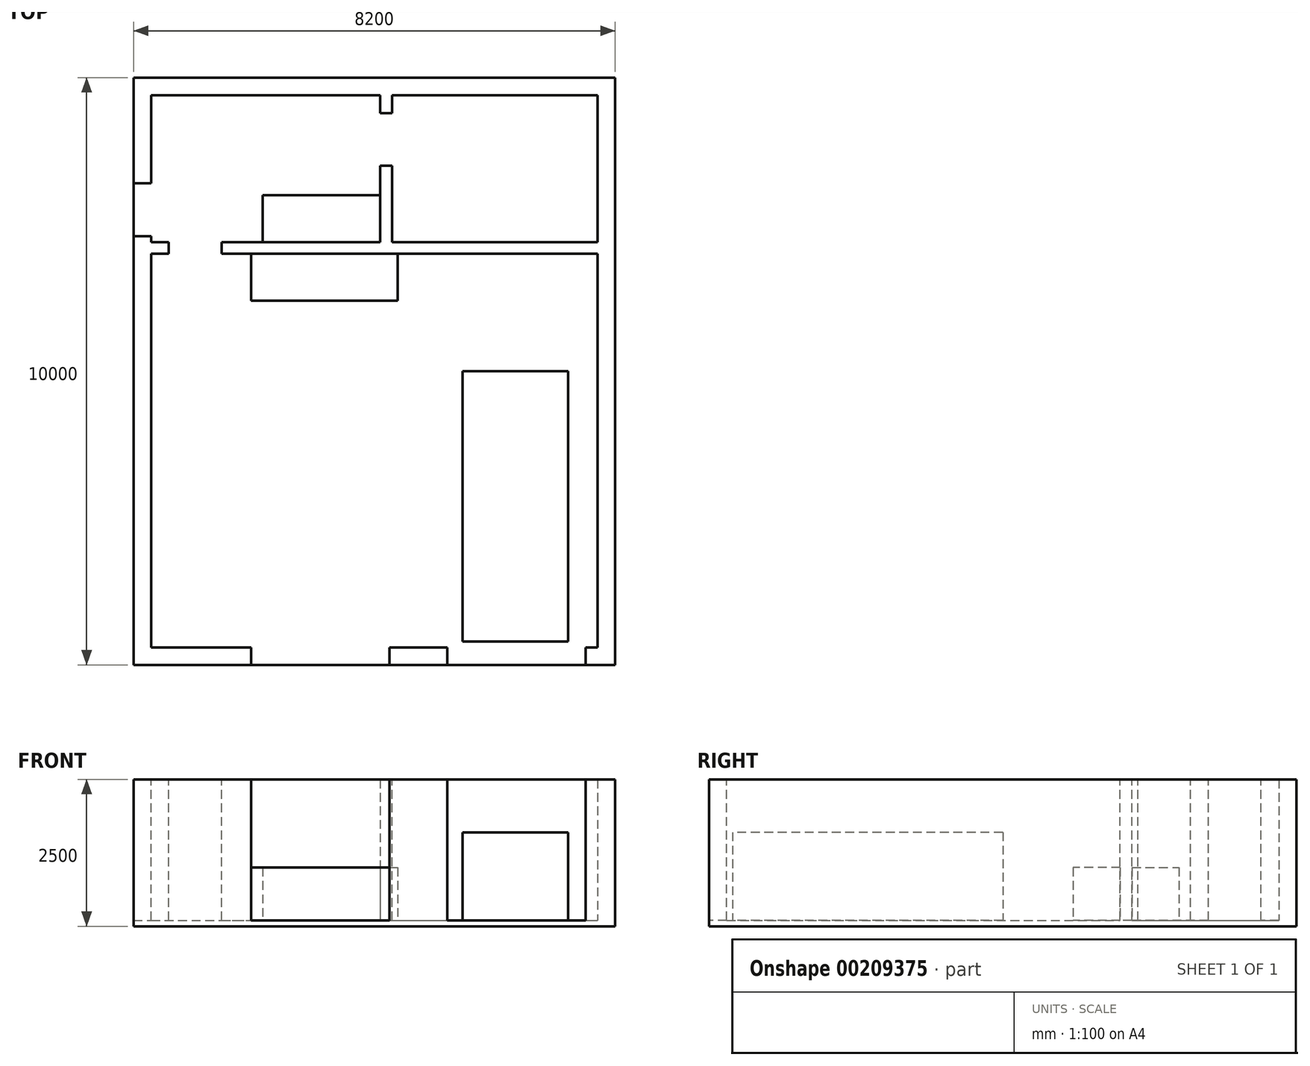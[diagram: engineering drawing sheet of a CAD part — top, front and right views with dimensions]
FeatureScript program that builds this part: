
annotation { "Feature Type Name" : "Feature", "Feature Type Description" : "" }
export const myFeature = defineFeature(function(context is Context, id is Id, definition is map)
    precondition{}
    {
        {
            var Q0;
            Q0=qCreatedBy(makeId("Top.planeOp"),FACE);
            var sketch = newSketch(context, id + "F0", { "sketchPlane" : qUnion([Q0])});
            skLineSegment(sketch, "E0.bottom", {"start": v(0, 0) * mm, "end": v(8200, 0) * mm});
            skLineSegment(sketch, "E0.top", {"start": v(0, 10000) * mm, "end": v(8200, 10000) * mm});
            skLineSegment(sketch, "E0.left", {"start": v(0, 0) * mm, "end": v(0, 10000) * mm});
            skLineSegment(sketch, "E0.right", {"start": v(8200, 0) * mm, "end": v(8200, 10000) * mm});
            skSolve(sketch);
        }
        {
            var Q0;
            Q0=makeQuery(id+"F0.imprint","IMPRINT",FACE,{"disambiguationData":[TD([[makeQuery(id+"F0.imprint","IMPRINT",EDGE,{"derivedFrom":sQuery(id+"F0.wireOp",EDGE,"E0.bottom")}),1.0]])]});
            var sketch = newSketch(context, id + "F1", { "sketchPlane" : qUnion([Q0])});
            skLineSegment(sketch, "E1.bottom", {"start": v(300, 300) * mm, "end": v(7900, 300) * mm});
            skLineSegment(sketch, "E1.top", {"start": v(300, 9700) * mm, "end": v(7900, 9700) * mm});
            skLineSegment(sketch, "E1.left", {"start": v(300, 300) * mm, "end": v(300, 9700) * mm});
            skLineSegment(sketch, "E1.right", {"start": v(7900, 300) * mm, "end": v(7900, 9700) * mm});
            skSolve(sketch);
        }
        {
            var Q0;
            Q0=makeQuery(id+"F0.imprint","IMPRINT",FACE,{"disambiguationData":[TD([[makeQuery(id+"F0.imprint","IMPRINT",EDGE,{"derivedFrom":sQuery(id+"F0.wireOp",EDGE,"E0.bottom")}),1.0]])]});
            var sketch = newSketch(context, id + "F2", { "sketchPlane" : qUnion([Q0])});
            skLineSegment(sketch, "E2", {"start": v(2000, 300) * mm, "end": v(2000, 0) * mm});
            skLineSegment(sketch, "E3", {"start": v(2000, 0) * mm, "end": v(4360, 0) * mm});
            skLineSegment(sketch, "E4", {"start": v(4360, 0) * mm, "end": v(4360, 300) * mm});
            skLineSegment(sketch, "E5", {"start": v(4360, 300) * mm, "end": v(2000, 300) * mm});
            skLineSegment(sketch, "E6.bottom", {"start": v(5340, 0) * mm, "end": v(7700, 0) * mm});
            skLineSegment(sketch, "E6.top", {"start": v(5340, 300) * mm, "end": v(7700, 300) * mm});
            skLineSegment(sketch, "E6.left", {"start": v(5340, 0) * mm, "end": v(5340, 300) * mm});
            skLineSegment(sketch, "E6.right", {"start": v(7700, 0) * mm, "end": v(7700, 300) * mm});
            skSolve(sketch);
        }
        {
            var Q0;
            Q0 = qSketchRegion(id + "F0", true);
            extrude(context, id + "F3", {"entities" : qUnion([Q0]), "oppositeDirection" : true, "depth" : 2500 * mm});
        }
        {
            var Q0;
            Q0 = qSketchRegion(id + "F1", true);
            extrude(context, id + "F4", {"entities" : qUnion([Q0]), "operationType" : NewBodyOperationType.REMOVE, "oppositeDirection" : true, "depth" : 2400 * mm});
        }
        {
            var Q0;
            Q0 = qSketchRegion(id + "F2", true);
            extrude(context, id + "F5", {"entities" : qUnion([Q0]), "operationType" : NewBodyOperationType.REMOVE, "oppositeDirection" : true, "depth" : 2400 * mm});
        }
        {
            var Q0;
            Q0=makeQuery(id+"F5.boolean.opBoolean","MERGE",FACE,{"derivedFrom":[makeQuery(id+"F4.boolean.opBoolean","COPY",FACE,{"derivedFrom":makeQuery(id+"F4.opExtrude","CAP_FACE",FACE,{"disambiguationData":[OSD([sQuery(id+"F1.wireOp",EDGE,"E1.bottom"),sQuery(id+"F1.wireOp",EDGE,"E1.top"),sQuery(id+"F1.wireOp",EDGE,"E1.left"),sQuery(id+"F1.wireOp",EDGE,"E1.right")])],"isStart":false})}),makeQuery(id+"F5.opExtrude","CAP_FACE",FACE,{"disambiguationData":[OSD([sQuery(id+"F2.wireOp",EDGE,"E2"),sQuery(id+"F2.wireOp",EDGE,"E3"),sQuery(id+"F2.wireOp",EDGE,"E4"),sQuery(id+"F2.wireOp",EDGE,"E5")])],"isStart":false}),makeQuery(id+"F5.opExtrude","CAP_FACE",FACE,{"disambiguationData":[OSD([sQuery(id+"F2.wireOp",EDGE,"E6.bottom"),sQuery(id+"F2.wireOp",EDGE,"E6.top"),sQuery(id+"F2.wireOp",EDGE,"E6.left"),sQuery(id+"F2.wireOp",EDGE,"E6.right")])],"isStart":false})]});
            var sketch = newSketch(context, id + "F6", { "sketchPlane" : qUnion([Q0])});
            skLineSegment(sketch, "E7.bottom", {"start": v(300, 7200) * mm, "end": v(7900, 7200) * mm});
            skLineSegment(sketch, "E7.top", {"start": v(300, 7000) * mm, "end": v(7900, 7000) * mm});
            skLineSegment(sketch, "E7.left", {"start": v(300, 7200) * mm, "end": v(300, 7000) * mm});
            skLineSegment(sketch, "E7.right", {"start": v(7900, 7200) * mm, "end": v(7900, 7000) * mm});
            skSolve(sketch);
        }
        {
            var Q0;
            Q0=makeQuery(id+"F6.imprint","IMPRINT",FACE,{"disambiguationData":[TD([[makeQuery(id+"F6.imprint","IMPRINT",EDGE,{"derivedFrom":sQuery(id+"F6.wireOp",EDGE,"E7.bottom")}),-1.0]])]});
            extrude(context, id + "F7", {"entities" : qUnion([Q0]), "operationType" : NewBodyOperationType.ADD, "depth" : 2400 * mm});
        }
        {
            var Q0;
            {var subQ0=sQuery(id+"F1.wireOp",EDGE,"E1.top");var subQ1=sQuery(id+"F1.wireOp",EDGE,"E1.left");var subQ2=sQuery(id+"F1.wireOp",EDGE,"E1.right");Q0=makeQuery(id+"F7.boolean.opBoolean","SPLIT",FACE,{"disambiguationData":[TD([makeQuery(id+"F4.boolean.opBoolean","COPY",FACE,{"derivedFrom":makeQuery(id+"F4.opExtrude","SWEPT_FACE",FACE,{"disambiguationData":[OSD([subQ0])]})})])],"derivedFrom":makeQuery(id+"F5.boolean.opBoolean","MERGE",FACE,{"derivedFrom":[makeQuery(id+"F4.boolean.opBoolean","COPY",FACE,{"derivedFrom":makeQuery(id+"F4.opExtrude","CAP_FACE",FACE,{"disambiguationData":[OSD([sQuery(id+"F1.wireOp",EDGE,"E1.bottom"),subQ0,subQ1,subQ2])],"isStart":false})}),makeQuery(id+"F5.opExtrude","CAP_FACE",FACE,{"disambiguationData":[OSD([sQuery(id+"F2.wireOp",EDGE,"E2"),sQuery(id+"F2.wireOp",EDGE,"E3"),sQuery(id+"F2.wireOp",EDGE,"E4"),sQuery(id+"F2.wireOp",EDGE,"E5")])],"isStart":false}),makeQuery(id+"F5.opExtrude","CAP_FACE",FACE,{"disambiguationData":[OSD([sQuery(id+"F2.wireOp",EDGE,"E6.bottom"),sQuery(id+"F2.wireOp",EDGE,"E6.top"),sQuery(id+"F2.wireOp",EDGE,"E6.left"),sQuery(id+"F2.wireOp",EDGE,"E6.right")])],"isStart":false})]})});}
            var sketch = newSketch(context, id + "F8", { "sketchPlane" : qUnion([Q0])});
            skLineSegment(sketch, "E8.bottom", {"start": v(4200, 9700) * mm, "end": v(4400, 9700) * mm});
            skLineSegment(sketch, "E8.top", {"start": v(4200, 7200) * mm, "end": v(4400, 7200) * mm});
            skLineSegment(sketch, "E8.left", {"start": v(4200, 9700) * mm, "end": v(4200, 7200) * mm});
            skLineSegment(sketch, "E8.right", {"start": v(4400, 9700) * mm, "end": v(4400, 7200) * mm});
            skSolve(sketch);
        }
        {
            var Q0;
            Q0 = qSketchRegion(id + "F8", true);
            extrude(context, id + "F9", {"entities" : qUnion([Q0]), "operationType" : NewBodyOperationType.ADD, "depth" : 2400 * mm});
        }
        {
            var Q0;
            {var subQ0=sQuery(id+"F0.wireOp",EDGE,"E0.right");var subQ1=sQuery(id+"F0.wireOp",EDGE,"E0.left");var subQ2=sQuery(id+"F0.wireOp",EDGE,"E0.top");var subQ3=sQuery(id+"F0.wireOp",EDGE,"E0.bottom");Q0=makeQuery(id+"F9.boolean.opBoolean","MERGE",FACE,{"derivedFrom":[makeQuery(id+"F7.boolean.opBoolean","MERGE",FACE,{"derivedFrom":[makeQuery(id+"F5.boolean.opBoolean","SPLIT",FACE,{"disambiguationData":[TD([makeQuery(id+"F3.opExtrude","SWEPT_FACE",FACE,{"disambiguationData":[OSD([subQ2])]})])],"derivedFrom":makeQuery(id+"F3.opExtrude","CAP_FACE",FACE,{"disambiguationData":[OSD([subQ3,subQ2,subQ1,subQ0])],"isStart":true})}),makeQuery(id+"F7.opExtrude","CAP_FACE",FACE,{"disambiguationData":[OSD([sQuery(id+"F6.wireOp",EDGE,"E7.bottom"),sQuery(id+"F6.wireOp",EDGE,"E7.top"),sQuery(id+"F6.wireOp",EDGE,"E7.left"),sQuery(id+"F6.wireOp",EDGE,"E7.right")])],"isStart":false})]}),makeQuery(id+"F9.opExtrude","CAP_FACE",FACE,{"disambiguationData":[OSD([sQuery(id+"F8.wireOp",EDGE,"E8.bottom"),sQuery(id+"F8.wireOp",EDGE,"E8.top"),sQuery(id+"F8.wireOp",EDGE,"E8.left"),sQuery(id+"F8.wireOp",EDGE,"E8.right")])],"isStart":false})]});}
            var sketch = newSketch(context, id + "F10", { "sketchPlane" : qUnion([Q0])});
            skLineSegment(sketch, "E9.bottom", {"start": v(0, 8200) * mm, "end": v(300, 8200) * mm});
            skLineSegment(sketch, "E9.top", {"start": v(0, 7300) * mm, "end": v(300, 7300) * mm});
            skLineSegment(sketch, "E9.left", {"start": v(0, 8200) * mm, "end": v(0, 7300) * mm});
            skLineSegment(sketch, "E9.right", {"start": v(300, 8200) * mm, "end": v(300, 7300) * mm});
            skLineSegment(sketch, "E10.bottom", {"start": v(600, 7200) * mm, "end": v(1500, 7200) * mm});
            skLineSegment(sketch, "E10.top", {"start": v(600, 7000) * mm, "end": v(1500, 7000) * mm});
            skLineSegment(sketch, "E10.left", {"start": v(600, 7200) * mm, "end": v(600, 7000) * mm});
            skLineSegment(sketch, "E10.right", {"start": v(1500, 7200) * mm, "end": v(1500, 7000) * mm});
            skLineSegment(sketch, "E11.bottom", {"start": v(4200, 9400) * mm, "end": v(4400, 9400) * mm});
            skLineSegment(sketch, "E11.top", {"start": v(4200, 8500) * mm, "end": v(4400, 8500) * mm});
            skLineSegment(sketch, "E11.left", {"start": v(4200, 9400) * mm, "end": v(4200, 8500) * mm});
            skLineSegment(sketch, "E11.right", {"start": v(4400, 9400) * mm, "end": v(4400, 8500) * mm});
            skSolve(sketch);
        }
        {
            var Q0;
            Q0=makeQuery(id+"F10.imprint","IMPRINT",FACE,{"disambiguationData":[TD([[makeQuery(id+"F10.imprint","IMPRINT",EDGE,{"derivedFrom":sQuery(id+"F10.wireOp",EDGE,"E10.bottom")}),-1.0]])]});
            var Q1;
            Q1=makeQuery(id+"F10.imprint","IMPRINT",FACE,{"disambiguationData":[TD([[makeQuery(id+"F10.imprint","IMPRINT",EDGE,{"derivedFrom":sQuery(id+"F10.wireOp",EDGE,"E11.bottom")}),-1.0]])]});
            var Q2;
            Q2=makeQuery(id+"F10.imprint","IMPRINT",FACE,{"disambiguationData":[TD([[makeQuery(id+"F10.imprint","IMPRINT",EDGE,{"derivedFrom":sQuery(id+"F10.wireOp",EDGE,"E9.bottom")}),-1.0]])]});
            extrude(context, id + "F11", {"entities" : qUnion([Q0, Q1, Q2]), "operationType" : NewBodyOperationType.REMOVE, "oppositeDirection" : true, "depth" : 2400 * mm});
        }
        {
            var Q0;
            {var subQ0=sQuery(id+"F1.wireOp",EDGE,"E1.top");var subQ1=makeQuery(id+"F4.boolean.opBoolean","COPY",FACE,{"derivedFrom":makeQuery(id+"F4.opExtrude","SWEPT_FACE",FACE,{"disambiguationData":[OSD([subQ0])]})});var subQ2=sQuery(id+"F1.wireOp",EDGE,"E1.right");var subQ3=makeQuery(id+"F4.boolean.opBoolean","COPY",FACE,{"derivedFrom":makeQuery(id+"F4.opExtrude","SWEPT_FACE",FACE,{"disambiguationData":[OSD([subQ2])]})});var subQ5=sQuery(id+"F1.wireOp",EDGE,"E1.left");var subQ6=makeQuery(id+"F4.boolean.opBoolean","COPY",FACE,{"derivedFrom":makeQuery(id+"F4.opExtrude","SWEPT_FACE",FACE,{"disambiguationData":[OSD([subQ5])]})});var subQ7=sQuery(id+"F2.wireOp",EDGE,"E6.right");var subQ8=sQuery(id+"F2.wireOp",EDGE,"E6.left");var subQ9=sQuery(id+"F2.wireOp",EDGE,"E4");var subQ10=sQuery(id+"F2.wireOp",EDGE,"E2");var subQ11=sQuery(id+"F1.wireOp",EDGE,"E1.bottom");var subQ12=makeQuery(id+"F5.boolean.opBoolean","MERGE",FACE,{"derivedFrom":[makeQuery(id+"F4.boolean.opBoolean","COPY",FACE,{"derivedFrom":makeQuery(id+"F4.opExtrude","CAP_FACE",FACE,{"disambiguationData":[OSD([subQ11,subQ0,subQ5,subQ2])],"isStart":false})}),makeQuery(id+"F5.opExtrude","CAP_FACE",FACE,{"disambiguationData":[OSD([subQ10,sQuery(id+"F2.wireOp",EDGE,"E3"),subQ9,sQuery(id+"F2.wireOp",EDGE,"E5")])],"isStart":false}),makeQuery(id+"F5.opExtrude","CAP_FACE",FACE,{"disambiguationData":[OSD([sQuery(id+"F2.wireOp",EDGE,"E6.bottom"),sQuery(id+"F2.wireOp",EDGE,"E6.top"),subQ8,subQ7])],"isStart":false})]});var subQ13=makeQuery(id+"F7.boolean.opBoolean","SPLIT",FACE,{"disambiguationData":[TD([subQ1])],"derivedFrom":subQ12});Q0=makeQuery(id+"F11.boolean.opBoolean","MERGE",FACE,{"derivedFrom":[makeQuery(id+"F7.boolean.opBoolean","SPLIT",FACE,{"disambiguationData":[TD([makeQuery(id+"F3.opExtrude","SWEPT_FACE",FACE,{"disambiguationData":[OSD([sQuery(id+"F0.wireOp",EDGE,"E0.bottom")])]})])],"derivedFrom":subQ12}),makeQuery(id+"F9.boolean.opBoolean","SPLIT",FACE,{"disambiguationData":[TD([subQ6])],"derivedFrom":subQ13}),makeQuery(id+"F9.boolean.opBoolean","SPLIT",FACE,{"disambiguationData":[TD([subQ3])],"derivedFrom":subQ13}),makeQuery(id+"F11.opExtrude","CAP_FACE",FACE,{"disambiguationData":[OSD([sQuery(id+"F10.wireOp",EDGE,"E9.bottom"),sQuery(id+"F10.wireOp",EDGE,"E9.top"),sQuery(id+"F10.wireOp",EDGE,"E9.left"),sQuery(id+"F10.wireOp",EDGE,"E9.right")])],"isStart":false}),makeQuery(id+"F11.opExtrude","CAP_FACE",FACE,{"disambiguationData":[OSD([sQuery(id+"F10.wireOp",EDGE,"E10.bottom"),sQuery(id+"F10.wireOp",EDGE,"E10.top"),sQuery(id+"F10.wireOp",EDGE,"E10.left"),sQuery(id+"F10.wireOp",EDGE,"E10.right")])],"isStart":false}),makeQuery(id+"F11.opExtrude","CAP_FACE",FACE,{"disambiguationData":[OSD([sQuery(id+"F10.wireOp",EDGE,"E11.bottom"),sQuery(id+"F10.wireOp",EDGE,"E11.top"),sQuery(id+"F10.wireOp",EDGE,"E11.left"),sQuery(id+"F10.wireOp",EDGE,"E11.right")])],"isStart":false})]});}
            var sketch = newSketch(context, id + "F12", { "sketchPlane" : qUnion([Q0])});
            skLineSegment(sketch, "E12.bottom", {"start": v(2200, 7200) * mm, "end": v(4200, 7200) * mm});
            skLineSegment(sketch, "E12.top", {"start": v(2200, 8000) * mm, "end": v(4200, 8000) * mm});
            skLineSegment(sketch, "E12.left", {"start": v(2200, 7200) * mm, "end": v(2200, 8000) * mm});
            skLineSegment(sketch, "E12.right", {"start": v(4200, 7200) * mm, "end": v(4200, 8000) * mm});
            skSolve(sketch);
        }
        {
            var Q0;
            Q0=makeQuery(id+"F12.imprint","IMPRINT",FACE,{"disambiguationData":[TD([[makeQuery(id+"F12.imprint","IMPRINT",EDGE,{"derivedFrom":sQuery(id+"F12.wireOp",EDGE,"E12.bottom")}),1.0]])]});
            extrude(context, id + "F13", {"entities" : qUnion([Q0]), "depth" : 900 * mm});
        }
        {
            var Q0;
            {var subQ0=sQuery(id+"F1.wireOp",EDGE,"E1.top");var subQ1=makeQuery(id+"F4.boolean.opBoolean","COPY",FACE,{"derivedFrom":makeQuery(id+"F4.opExtrude","SWEPT_FACE",FACE,{"disambiguationData":[OSD([subQ0])]})});var subQ2=sQuery(id+"F1.wireOp",EDGE,"E1.right");var subQ3=makeQuery(id+"F4.boolean.opBoolean","COPY",FACE,{"derivedFrom":makeQuery(id+"F4.opExtrude","SWEPT_FACE",FACE,{"disambiguationData":[OSD([subQ2])]})});var subQ5=sQuery(id+"F1.wireOp",EDGE,"E1.left");var subQ6=makeQuery(id+"F4.boolean.opBoolean","COPY",FACE,{"derivedFrom":makeQuery(id+"F4.opExtrude","SWEPT_FACE",FACE,{"disambiguationData":[OSD([subQ5])]})});var subQ7=sQuery(id+"F2.wireOp",EDGE,"E6.right");var subQ8=sQuery(id+"F2.wireOp",EDGE,"E6.left");var subQ9=sQuery(id+"F2.wireOp",EDGE,"E4");var subQ10=sQuery(id+"F2.wireOp",EDGE,"E2");var subQ11=sQuery(id+"F1.wireOp",EDGE,"E1.bottom");var subQ12=makeQuery(id+"F5.boolean.opBoolean","MERGE",FACE,{"derivedFrom":[makeQuery(id+"F4.boolean.opBoolean","COPY",FACE,{"derivedFrom":makeQuery(id+"F4.opExtrude","CAP_FACE",FACE,{"disambiguationData":[OSD([subQ11,subQ0,subQ5,subQ2])],"isStart":false})}),makeQuery(id+"F5.opExtrude","CAP_FACE",FACE,{"disambiguationData":[OSD([subQ10,sQuery(id+"F2.wireOp",EDGE,"E3"),subQ9,sQuery(id+"F2.wireOp",EDGE,"E5")])],"isStart":false}),makeQuery(id+"F5.opExtrude","CAP_FACE",FACE,{"disambiguationData":[OSD([sQuery(id+"F2.wireOp",EDGE,"E6.bottom"),sQuery(id+"F2.wireOp",EDGE,"E6.top"),subQ8,subQ7])],"isStart":false})]});var subQ13=makeQuery(id+"F7.boolean.opBoolean","SPLIT",FACE,{"disambiguationData":[TD([subQ1])],"derivedFrom":subQ12});Q0=makeQuery(id+"F11.boolean.opBoolean","MERGE",FACE,{"derivedFrom":[makeQuery(id+"F7.boolean.opBoolean","SPLIT",FACE,{"disambiguationData":[TD([makeQuery(id+"F3.opExtrude","SWEPT_FACE",FACE,{"disambiguationData":[OSD([sQuery(id+"F0.wireOp",EDGE,"E0.bottom")])]})])],"derivedFrom":subQ12}),makeQuery(id+"F9.boolean.opBoolean","SPLIT",FACE,{"disambiguationData":[TD([subQ6])],"derivedFrom":subQ13}),makeQuery(id+"F9.boolean.opBoolean","SPLIT",FACE,{"disambiguationData":[TD([subQ3])],"derivedFrom":subQ13}),makeQuery(id+"F11.opExtrude","CAP_FACE",FACE,{"disambiguationData":[OSD([sQuery(id+"F10.wireOp",EDGE,"E9.bottom"),sQuery(id+"F10.wireOp",EDGE,"E9.top"),sQuery(id+"F10.wireOp",EDGE,"E9.left"),sQuery(id+"F10.wireOp",EDGE,"E9.right")])],"isStart":false}),makeQuery(id+"F11.opExtrude","CAP_FACE",FACE,{"disambiguationData":[OSD([sQuery(id+"F10.wireOp",EDGE,"E10.bottom"),sQuery(id+"F10.wireOp",EDGE,"E10.top"),sQuery(id+"F10.wireOp",EDGE,"E10.left"),sQuery(id+"F10.wireOp",EDGE,"E10.right")])],"isStart":false}),makeQuery(id+"F11.opExtrude","CAP_FACE",FACE,{"disambiguationData":[OSD([sQuery(id+"F10.wireOp",EDGE,"E11.bottom"),sQuery(id+"F10.wireOp",EDGE,"E11.top"),sQuery(id+"F10.wireOp",EDGE,"E11.left"),sQuery(id+"F10.wireOp",EDGE,"E11.right")])],"isStart":false})]});}
            var sketch = newSketch(context, id + "F14", { "sketchPlane" : qUnion([Q0])});
            skLineSegment(sketch, "E13.bottom", {"start": v(5600, 5000) * mm, "end": v(7400, 5000) * mm});
            skLineSegment(sketch, "E13.top", {"start": v(5600, 400) * mm, "end": v(7400, 400) * mm});
            skLineSegment(sketch, "E13.left", {"start": v(5600, 5000) * mm, "end": v(5600, 400) * mm});
            skLineSegment(sketch, "E13.right", {"start": v(7400, 5000) * mm, "end": v(7400, 400) * mm});
            skSolve(sketch);
        }
        {
            var Q0;
            Q0 = qSketchRegion(id + "F14", true);
            extrude(context, id + "F15", {"entities" : qUnion([Q0]), "depth" : 1500 * mm});
        }
        {
            var Q0;
            {var subQ0=sQuery(id+"F1.wireOp",EDGE,"E1.top");var subQ1=makeQuery(id+"F4.boolean.opBoolean","COPY",FACE,{"derivedFrom":makeQuery(id+"F4.opExtrude","SWEPT_FACE",FACE,{"disambiguationData":[OSD([subQ0])]})});var subQ2=sQuery(id+"F1.wireOp",EDGE,"E1.right");var subQ3=makeQuery(id+"F4.boolean.opBoolean","COPY",FACE,{"derivedFrom":makeQuery(id+"F4.opExtrude","SWEPT_FACE",FACE,{"disambiguationData":[OSD([subQ2])]})});var subQ5=sQuery(id+"F1.wireOp",EDGE,"E1.left");var subQ6=makeQuery(id+"F4.boolean.opBoolean","COPY",FACE,{"derivedFrom":makeQuery(id+"F4.opExtrude","SWEPT_FACE",FACE,{"disambiguationData":[OSD([subQ5])]})});var subQ7=sQuery(id+"F2.wireOp",EDGE,"E6.right");var subQ8=sQuery(id+"F2.wireOp",EDGE,"E6.left");var subQ9=sQuery(id+"F2.wireOp",EDGE,"E4");var subQ10=sQuery(id+"F2.wireOp",EDGE,"E2");var subQ11=sQuery(id+"F1.wireOp",EDGE,"E1.bottom");var subQ12=makeQuery(id+"F5.boolean.opBoolean","MERGE",FACE,{"derivedFrom":[makeQuery(id+"F4.boolean.opBoolean","COPY",FACE,{"derivedFrom":makeQuery(id+"F4.opExtrude","CAP_FACE",FACE,{"disambiguationData":[OSD([subQ11,subQ0,subQ5,subQ2])],"isStart":false})}),makeQuery(id+"F5.opExtrude","CAP_FACE",FACE,{"disambiguationData":[OSD([subQ10,sQuery(id+"F2.wireOp",EDGE,"E3"),subQ9,sQuery(id+"F2.wireOp",EDGE,"E5")])],"isStart":false}),makeQuery(id+"F5.opExtrude","CAP_FACE",FACE,{"disambiguationData":[OSD([sQuery(id+"F2.wireOp",EDGE,"E6.bottom"),sQuery(id+"F2.wireOp",EDGE,"E6.top"),subQ8,subQ7])],"isStart":false})]});var subQ13=makeQuery(id+"F7.boolean.opBoolean","SPLIT",FACE,{"disambiguationData":[TD([subQ1])],"derivedFrom":subQ12});Q0=makeQuery(id+"F11.boolean.opBoolean","MERGE",FACE,{"derivedFrom":[makeQuery(id+"F7.boolean.opBoolean","SPLIT",FACE,{"disambiguationData":[TD([makeQuery(id+"F3.opExtrude","SWEPT_FACE",FACE,{"disambiguationData":[OSD([sQuery(id+"F0.wireOp",EDGE,"E0.bottom")])]})])],"derivedFrom":subQ12}),makeQuery(id+"F9.boolean.opBoolean","SPLIT",FACE,{"disambiguationData":[TD([subQ6])],"derivedFrom":subQ13}),makeQuery(id+"F9.boolean.opBoolean","SPLIT",FACE,{"disambiguationData":[TD([subQ3])],"derivedFrom":subQ13}),makeQuery(id+"F11.opExtrude","CAP_FACE",FACE,{"disambiguationData":[OSD([sQuery(id+"F10.wireOp",EDGE,"E9.bottom"),sQuery(id+"F10.wireOp",EDGE,"E9.top"),sQuery(id+"F10.wireOp",EDGE,"E9.left"),sQuery(id+"F10.wireOp",EDGE,"E9.right")])],"isStart":false}),makeQuery(id+"F11.opExtrude","CAP_FACE",FACE,{"disambiguationData":[OSD([sQuery(id+"F10.wireOp",EDGE,"E10.bottom"),sQuery(id+"F10.wireOp",EDGE,"E10.top"),sQuery(id+"F10.wireOp",EDGE,"E10.left"),sQuery(id+"F10.wireOp",EDGE,"E10.right")])],"isStart":false}),makeQuery(id+"F11.opExtrude","CAP_FACE",FACE,{"disambiguationData":[OSD([sQuery(id+"F10.wireOp",EDGE,"E11.bottom"),sQuery(id+"F10.wireOp",EDGE,"E11.top"),sQuery(id+"F10.wireOp",EDGE,"E11.left"),sQuery(id+"F10.wireOp",EDGE,"E11.right")])],"isStart":false})]});}
            var sketch = newSketch(context, id + "F16", { "sketchPlane" : qUnion([Q0])});
            skLineSegment(sketch, "E14.bottom", {"start": v(2000, 7000) * mm, "end": v(4500, 7000) * mm});
            skLineSegment(sketch, "E14.top", {"start": v(2000, 6200) * mm, "end": v(4500, 6200) * mm});
            skLineSegment(sketch, "E14.left", {"start": v(2000, 7000) * mm, "end": v(2000, 6200) * mm});
            skLineSegment(sketch, "E14.right", {"start": v(4500, 7000) * mm, "end": v(4500, 6200) * mm});
            skSolve(sketch);
        }
        {
            var Q0;
            Q0 = qSketchRegion(id + "F16", true);
            extrude(context, id + "F17", {"entities" : qUnion([Q0]), "depth" : 900 * mm});
        }
    });
